# Revit family: Console Lavatory_TOTO_LW4704
name_source: partatom
category: 衛生器具
revit_build: Autodesk Revit 2018 (Build: 20170223_1515(x64)
units: mm (PartAtom-declared; Revit-internal decimal feet)

## family parameters
OmniClass タイトル = Sanitary, Laundry, and Cleaning Equipment
OmniClass 番号 = 23.45.00.00
パーツ タイプ = 標準
ロード時にボイドで切り取り = いいえ
丸型コネクタ寸法 = 直径を使用
作業面ベース = いいえ
共有 = いいえ
常に垂直 = はい
部屋計算ポイント = いいえ

## types (1)
- Console Lavatory_TOTO_LW4704
    Finish = basin_material
    Height = 177  [stored 0.580709 ft]
    Length = 420  [stored 1.37795 ft]
    TOTO AsiaOceania = L4704E
    TOTO China = LW4704VB
    TOTO Europe = L4704E
    TOTO HongKong = L4704E
    TOTO India = L4704E
    TOTO Russia = L4704E
    TOTO Taiwan = L4704E
    TOTO Thailand = L4704E
    TOTO USA = LT477G
    TOTO Vietnam = L4704
    Width = 460  [stored 1.50919 ft]
    排気配管 = いいえ
    排水配管 = いいえ
    水配管 = いいえ
    温水配管 = いいえ
    製造元 = TOTO Ltd.
    説明 = Console Lavatory/桌上式洗脸盆

note: [stored X ft] marks values corroborated as IEEE doubles in the binary element streams (Revit-internal decimal feet)

## geometry (parser evidence)
native form markers: Sweep x2
no freeform markers — native parametric forms only
